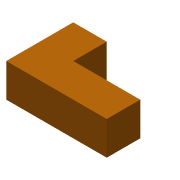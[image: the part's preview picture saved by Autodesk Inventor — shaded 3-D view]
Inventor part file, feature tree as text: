
AUTODESK INVENTOR PART (.ipt)
format: ipt  version: 2015 (Build 190159000, 159)  size: 75,776 bytes
history: native  units: in
note: dims shown in document units (in); Inventor stores cm internally (conversion verified against a paired STEP export)
features: extrude x1, sketch x1
ambient origin geometry x8: Origin, YZ Plane, XZ Plane, XY Plane, X Axis, Y Axis, Z Axis, Center Point
bodies: Solid1 (feature_tree)
feature tree (2):
  extrude  "Extrusion1"  Depth=2.0in
  sketch  "Sketch1"  dims[d0=3.0in d1=2.0in d2=1.0in d3=1.0in d4=1.0in d5=0.0in]
